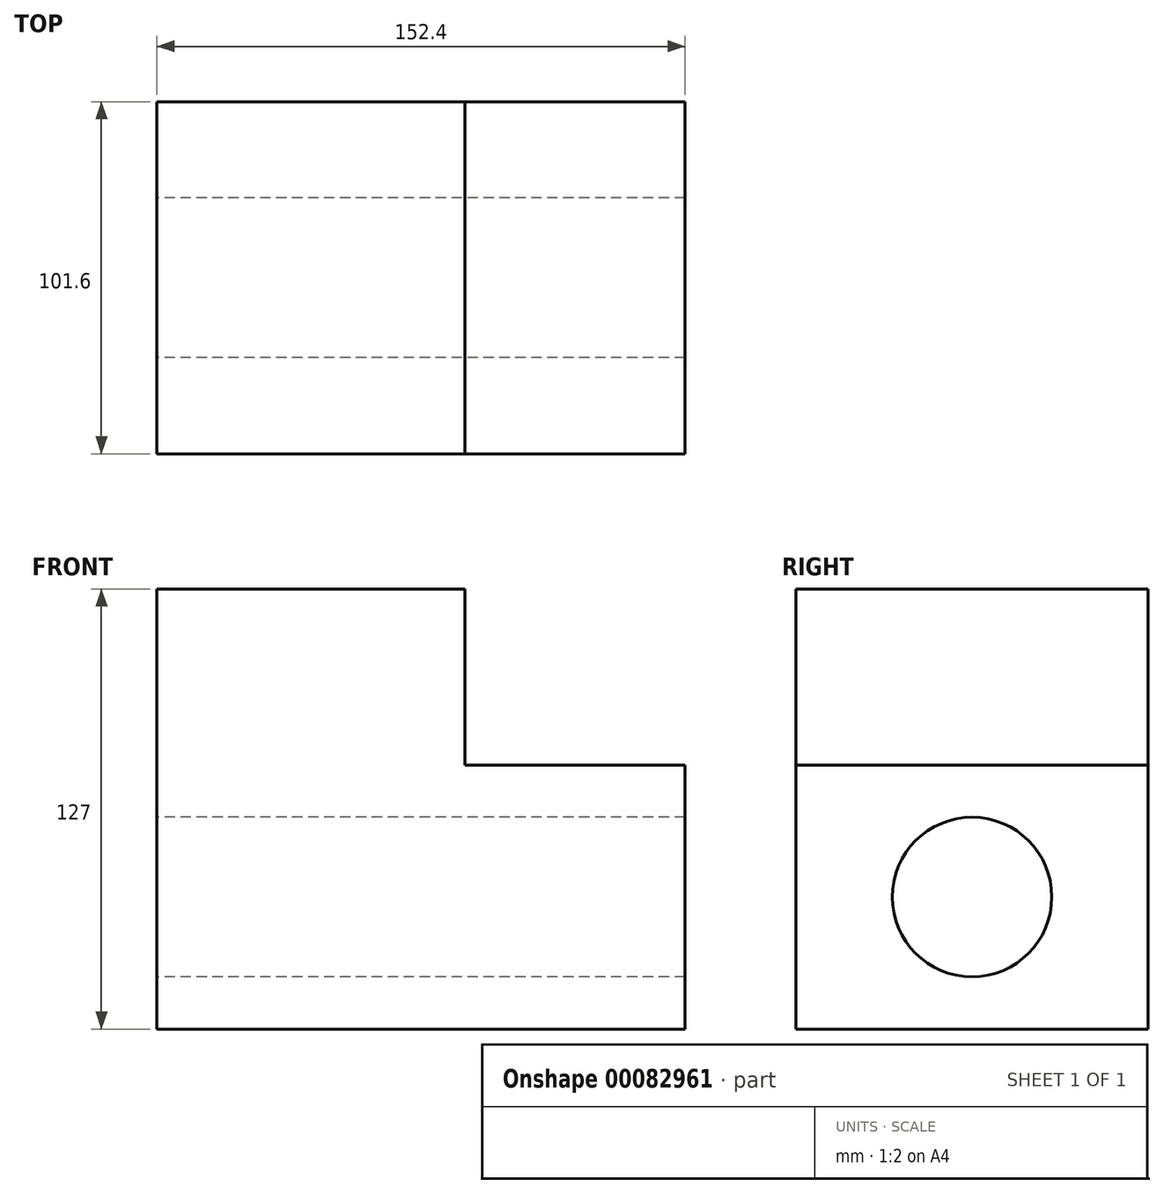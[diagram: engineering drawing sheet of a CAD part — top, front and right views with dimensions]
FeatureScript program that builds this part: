
annotation { "Feature Type Name" : "Feature", "Feature Type Description" : "" }
export const myFeature = defineFeature(function(context is Context, id is Id, definition is map)
    precondition{}
    {
        {
            var Q0;
            Q0=qCreatedBy(makeId("Top.planeOp"),FACE);
            var sketch = newSketch(context, id + "F0", { "sketchPlane" : qUnion([Q0])});
            skLineSegment(sketch, "E0.bottom", {"start": v(-48.76, 60.3) * mm, "end": v(103.64, 60.3) * mm});
            skLineSegment(sketch, "E0.top", {"start": v(-48.76, -41.3) * mm, "end": v(103.64, -41.3) * mm});
            skLineSegment(sketch, "E0.left", {"start": v(-48.76, 60.3) * mm, "end": v(-48.76, -41.3) * mm});
            skLineSegment(sketch, "E0.right", {"start": v(103.64, 60.3) * mm, "end": v(103.64, -41.3) * mm});
            skSolve(sketch);
        }
        {
            var Q0;
            Q0=makeQuery(id+"F0.imprint","IMPRINT",FACE,{"disambiguationData":[TD([[makeQuery(id+"F0.imprint","IMPRINT",EDGE,{"derivedFrom":sQuery(id+"F0.wireOp",EDGE,"E0.bottom")}),-1.0]])]});
            extrude(context, id + "F1", {"entities" : qUnion([Q0]), "depth" : 127 * mm});
        }
        {
            var Q0;
            Q0=makeQuery(id+"F1.opExtrude","SWEPT_FACE",FACE,{"disambiguationData":[OSD([sQuery(id+"F0.wireOp",EDGE,"E0.top")])]});
            var sketch = newSketch(context, id + "F2", { "sketchPlane" : qUnion([Q0])});
            skLineSegment(sketch, "E1.bottom", {"start": v(103.64, 127) * mm, "end": v(40.14, 127) * mm});
            skLineSegment(sketch, "E1.top", {"start": v(103.64, 76.2) * mm, "end": v(40.14, 76.2) * mm});
            skLineSegment(sketch, "E1.left", {"start": v(103.64, 127) * mm, "end": v(103.64, 76.2) * mm});
            skLineSegment(sketch, "E1.right", {"start": v(40.14, 127) * mm, "end": v(40.14, 76.2) * mm});
            skSolve(sketch);
        }
        {
            var Q0;
            Q0=makeQuery(id+"F2.imprint","IMPRINT",FACE,{"disambiguationData":[TD([[makeQuery(id+"F2.imprint","IMPRINT",EDGE,{"derivedFrom":sQuery(id+"F2.wireOp",EDGE,"E1.bottom")}),-1.0]])]});
            extrude(context, id + "F3", {"entities" : qUnion([Q0]), "operationType" : NewBodyOperationType.REMOVE, "oppositeDirection" : true, "depth" : 103.88 * mm});
        }
        {
            var Q0;
            Q0=makeQuery(id+"F1.opExtrude","SWEPT_FACE",FACE,{"disambiguationData":[OSD([sQuery(id+"F0.wireOp",EDGE,"E0.left")])]});
            var sketch = newSketch(context, id + "F4", { "sketchPlane" : qUnion([Q0])});
            skCircle(sketch, "E2", {"center": v(-9.5, 38.1) * mm, "radius": 23.01 * mm});
            skSolve(sketch);
        }
        {
            var Q0;
            Q0=makeQuery(id+"F4.imprint","IMPRINT",FACE,{"disambiguationData":[TD([[makeQuery(id+"F4.imprint","IMPRINT",EDGE,{"derivedFrom":sQuery(id+"F4.wireOp",EDGE,"E2")}),1.0]])]});
            var sketch = newSketch(context, id + "F5", { "sketchPlane" : qUnion([Q0])});
            skSolve(sketch);
        }
        {
            var Q0;
            Q0 = qSketchRegion(id + "F5", true);
            var Q1;
            Q1=makeQuery(id+"F4.imprint","IMPRINT",FACE,{"disambiguationData":[TD([[makeQuery(id+"F4.imprint","IMPRINT",EDGE,{"derivedFrom":sQuery(id+"F4.wireOp",EDGE,"E2")}),1.0]])]});
            extrude(context, id + "F6", {"entities" : qUnion([Q0, Q1]), "operationType" : NewBodyOperationType.REMOVE, "endBound" : BoundingType.THROUGH_ALL, "oppositeDirection" : true, "depth" : 25.4 * mm});
        }
    });
